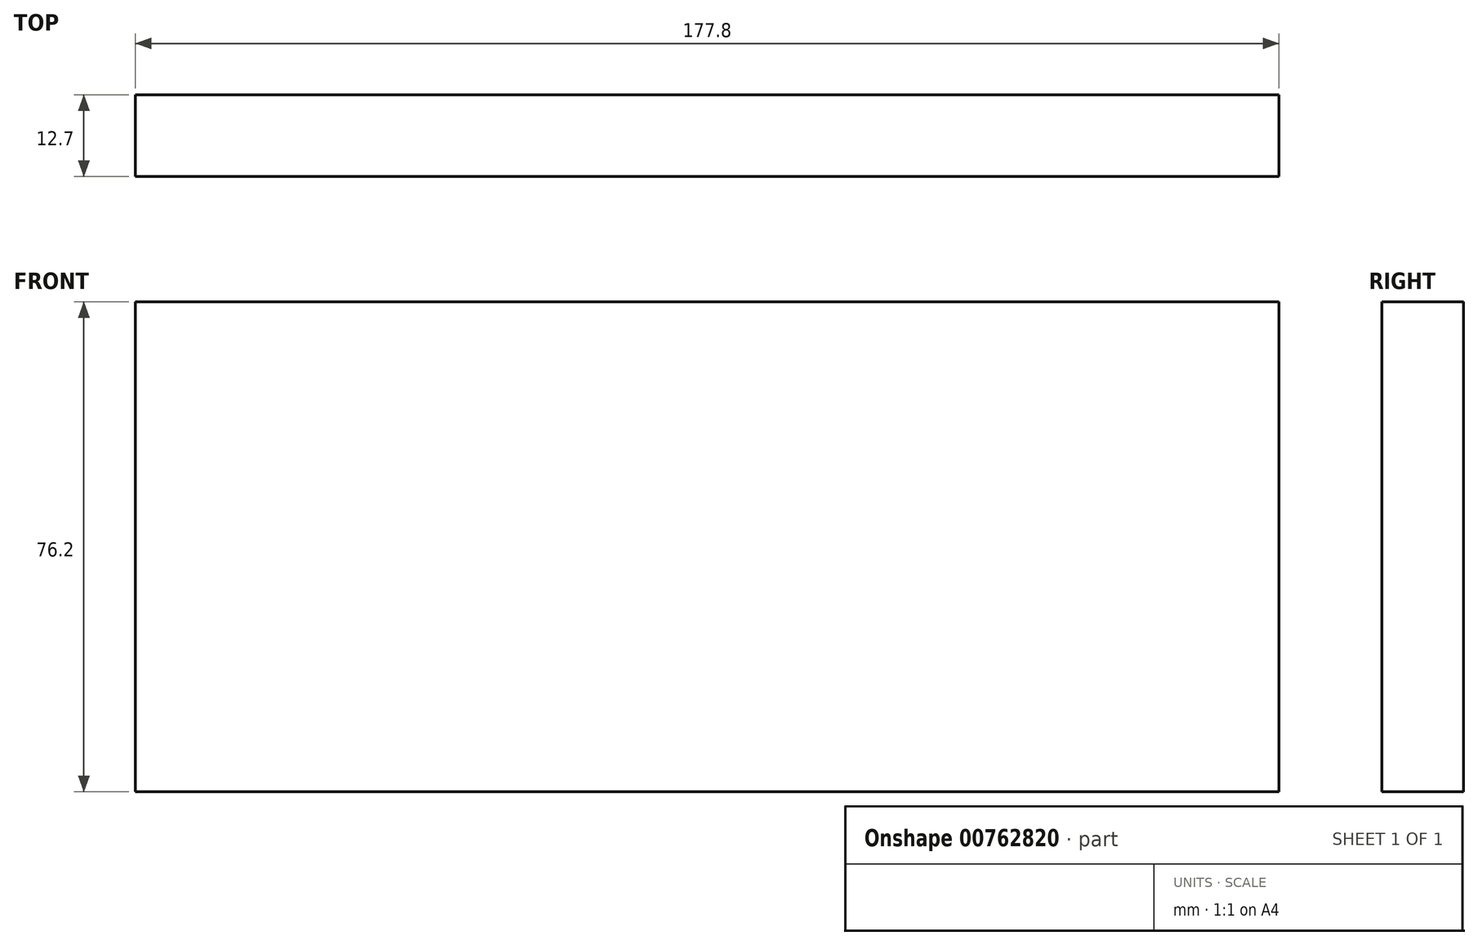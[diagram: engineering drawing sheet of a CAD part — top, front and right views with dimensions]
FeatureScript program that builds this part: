
annotation { "Feature Type Name" : "Feature", "Feature Type Description" : "" }
export const myFeature = defineFeature(function(context is Context, id is Id, definition is map)
    precondition{}
    {
        {
            var Q0;
            Q0=qCreatedBy(makeId("Top.planeOp"),FACE);
            var sketch = newSketch(context, id + "F0", { "sketchPlane" : qUnion([Q0])});
            skLineSegment(sketch, "E0.bottom", {"start": v(-63.99, -12.7) * mm, "end": v(113.81, -12.7) * mm});
            skLineSegment(sketch, "E0.top", {"start": v(-63.99, 0) * mm, "end": v(113.81, 0) * mm});
            skLineSegment(sketch, "E0.left", {"start": v(-63.99, -12.7) * mm, "end": v(-63.99, 0) * mm});
            skLineSegment(sketch, "E0.right", {"start": v(113.81, -12.7) * mm, "end": v(113.81, 0) * mm});
            skSolve(sketch);
        }
        {
            var Q0;
            Q0 = qSketchRegion(id + "F0", true);
            extrude(context, id + "F1", {"entities" : qUnion([Q0]), "depth" : 76.2 * mm, "offsetDistance" : 25.4 * mm});
        }
    });
